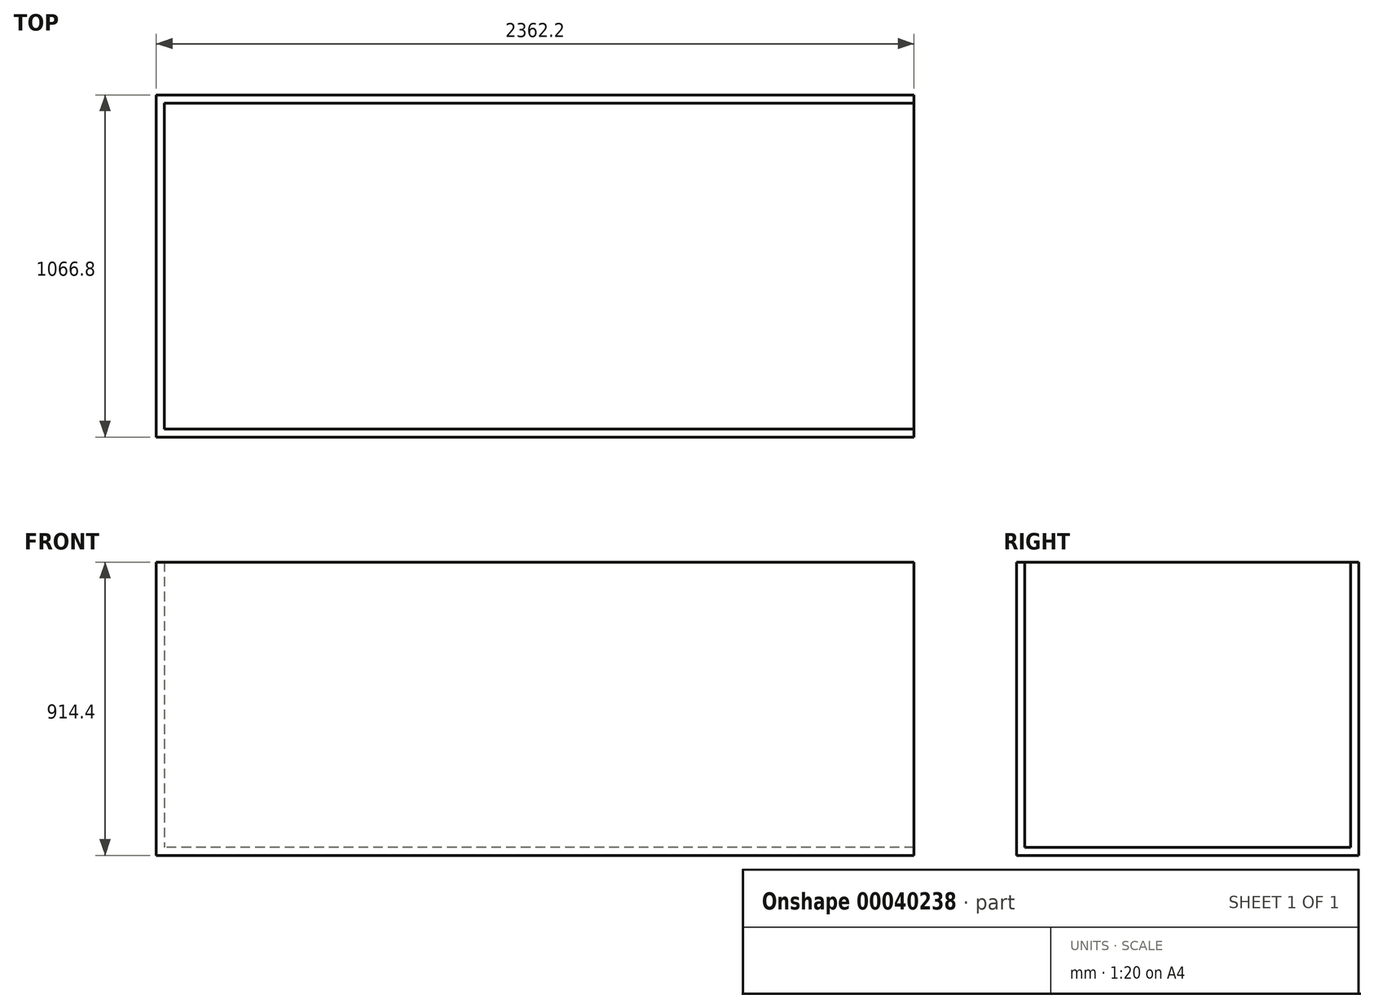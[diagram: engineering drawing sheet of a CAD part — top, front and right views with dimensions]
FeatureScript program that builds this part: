
annotation { "Feature Type Name" : "Feature", "Feature Type Description" : "" }
export const myFeature = defineFeature(function(context is Context, id is Id, definition is map)
    precondition{}
    {
        {
            var Q0;
            Q0=qCreatedBy(makeId("Top.planeOp"),FACE);
            var sketch = newSketch(context, id + "F0", { "sketchPlane" : qUnion([Q0])});
            skLineSegment(sketch, "E0.rect.bottom", {"start": v(1168.4, 508) * mm, "end": v(-1168.4, 508) * mm});
            skLineSegment(sketch, "E0.rect.top", {"start": v(1168.4, -508) * mm, "end": v(-1168.4, -508) * mm});
            skLineSegment(sketch, "E0.rect.left", {"start": v(1168.4, 508) * mm, "end": v(1168.4, -508) * mm});
            skLineSegment(sketch, "E0.rect.right", {"start": v(-1168.4, 508) * mm, "end": v(-1168.4, -508) * mm});
            skPoint(sketch, "E0.rect.middle", {"position": v(0, 0) * mm});
            skLineSegment(sketch, "E1.0", {"start": v(1168.4, -533.4) * mm, "end": v(-1193.8, -533.4) * mm});
            skLineSegment(sketch, "E1.1", {"start": v(-1193.8, 533.4) * mm, "end": v(-1193.8, -533.4) * mm});
            skLineSegment(sketch, "E1.2", {"start": v(1168.4, 533.4) * mm, "end": v(-1193.8, 533.4) * mm});
            skLineSegment(sketch, "E2", {"start": v(1168.4, 508) * mm, "end": v(1168.4, 533.4) * mm});
            skLineSegment(sketch, "E3", {"start": v(1168.4, -508) * mm, "end": v(1168.4, -533.4) * mm});
            skSolve(sketch);
        }
        {
            var Q0;
            Q0=makeQuery(id+"F0.imprint","IMPRINT",FACE,{"disambiguationData":[TD([[makeQuery(id+"F0.imprint","IMPRINT",EDGE,{"derivedFrom":sQuery(id+"F0.wireOp",EDGE,"E0.rect.bottom")}),-1.0]])]});
            extrude(context, id + "F1", {"entities" : qUnion([Q0]), "depth" : 914.4 * mm});
        }
        {
            var Q0;
            Q0=makeQuery(id+"F0.imprint","IMPRINT",FACE,{"disambiguationData":[TD([[makeQuery(id+"F0.imprint","IMPRINT",EDGE,{"derivedFrom":sQuery(id+"F0.wireOp",EDGE,"E0.rect.bottom")}),1.0]])]});
            extrude(context, id + "F2", {"entities" : qUnion([Q0]), "operationType" : NewBodyOperationType.ADD, "depth" : 25.4 * mm});
        }
    });
